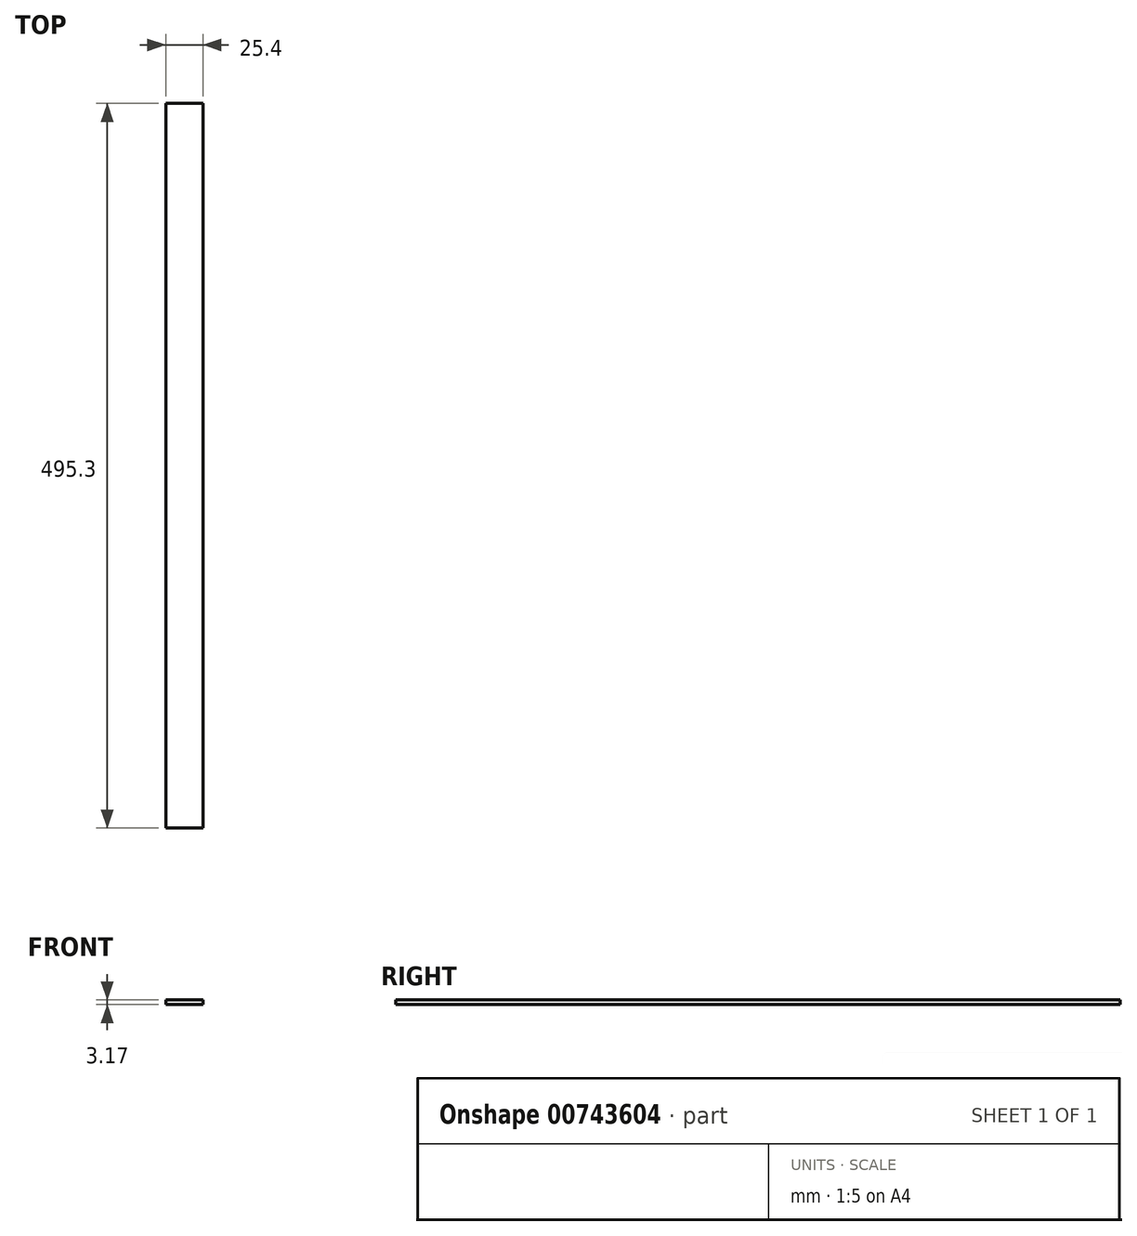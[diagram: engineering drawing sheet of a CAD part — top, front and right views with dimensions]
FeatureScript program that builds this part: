
annotation { "Feature Type Name" : "Feature", "Feature Type Description" : "" }
export const myFeature = defineFeature(function(context is Context, id is Id, definition is map)
    precondition{}
    {
        {
            var Q0;
            Q0=qCreatedBy(makeId("Top.planeOp"),FACE);
            var sketch = newSketch(context, id + "F0", { "sketchPlane" : qUnion([Q0])});
            skLineSegment(sketch, "E0", {"start": v(32.28, -249.1) * mm, "end": v(32.28, 246.2) * mm});
            skLineSegment(sketch, "E1", {"start": v(32.28, 246.2) * mm, "end": v(57.68, 246.2) * mm});
            skLineSegment(sketch, "E2", {"start": v(57.68, 246.2) * mm, "end": v(57.68, -249.1) * mm});
            skLineSegment(sketch, "E3", {"start": v(57.68, -249.1) * mm, "end": v(32.28, -249.1) * mm});
            skSolve(sketch);
        }
        {
            var Q0;
            Q0=makeQuery(id+"F0.imprint","IMPRINT",FACE,{"disambiguationData":[TD([[makeQuery(id+"F0.imprint","IMPRINT",EDGE,{"derivedFrom":sQuery(id+"F0.wireOp",EDGE,"E0")}),-1.0]])]});
            extrude(context, id + "F1", {"entities" : qUnion([Q0]), "depth" : 3.17 * mm, "offsetDistance" : 25.4 * mm});
        }
    });
